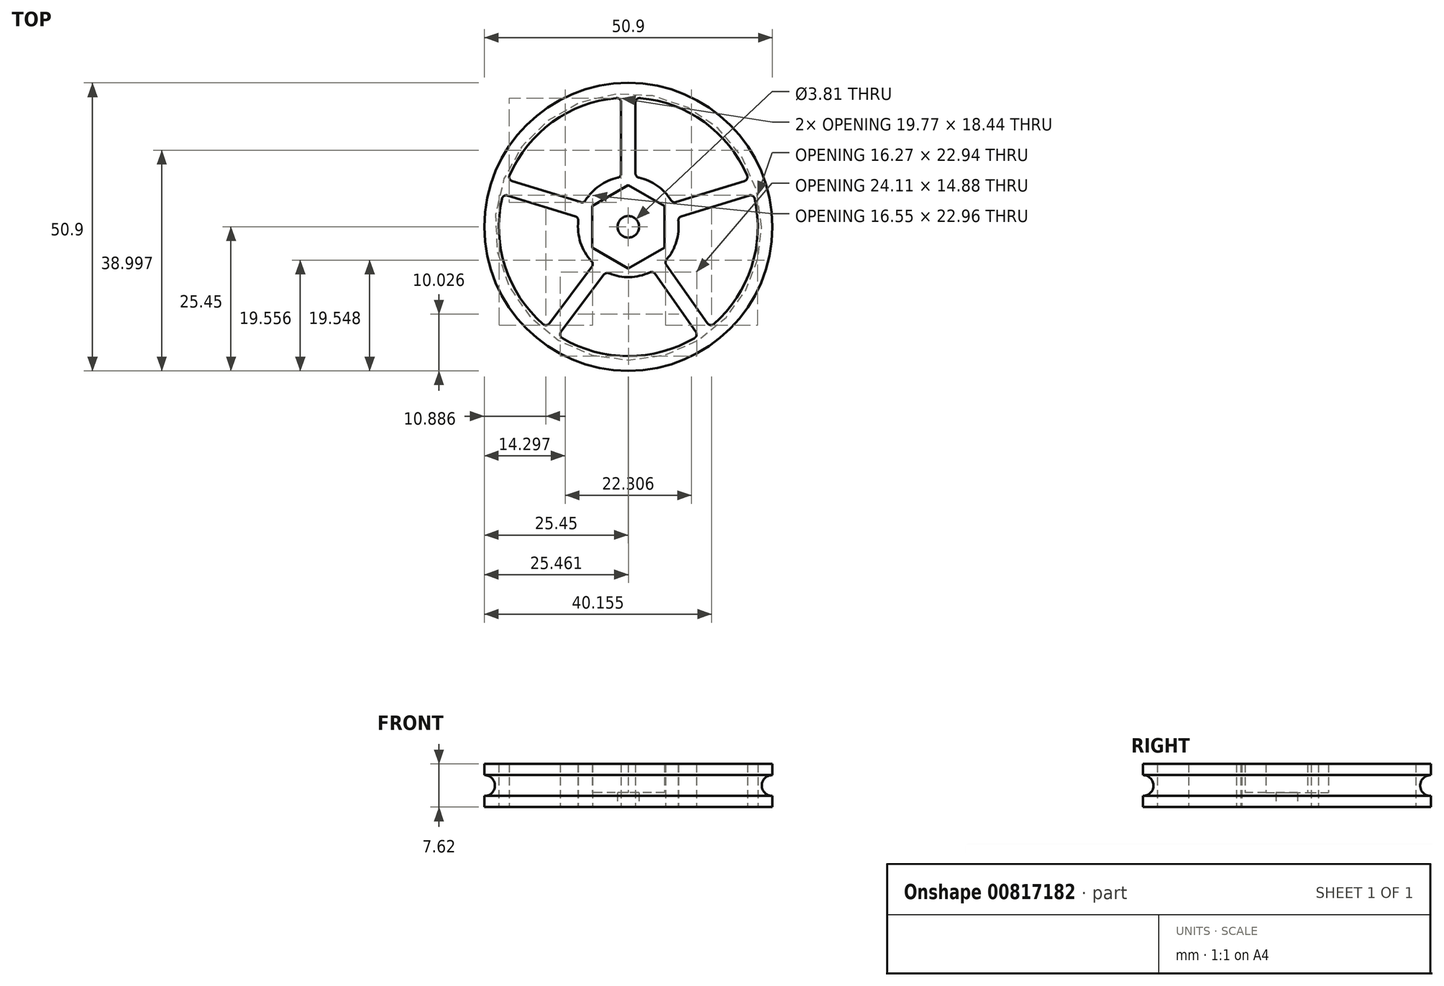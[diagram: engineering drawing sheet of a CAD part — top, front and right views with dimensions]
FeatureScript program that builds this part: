
annotation { "Feature Type Name" : "Feature", "Feature Type Description" : "" }
export const myFeature = defineFeature(function(context is Context, id is Id, definition is map)
    precondition{}
    {
        {
            var Q0;
            Q0=qCreatedBy(makeId("Top.planeOp"),FACE);
            var sketch = newSketch(context, id + "F0", { "sketchPlane" : qUnion([Q0])});
            skCircle(sketch, "E0", {"center": v(0, 0) * mm, "radius": 25.45 * mm});
            skArc(sketch, "E1", {"start": v(-22.32, 4.98) * mm, "mid": v(-21.74, -7.1) * mm, "end": v(-15.07, -17.2) * mm});
            skArc(sketch, "E2", {"start": v(-1.87, 8.7) * mm, "mid": v(-5.12, 7.27) * mm, "end": v(-7.56, 4.69) * mm});
            skArc(sketch, "E3.cCircle", {"start": v(-22.12, 5.78) * mm, "mid": v(-21.74, -7.1) * mm, "end": v(-14.45, -17.72) * mm, "construction": true});
            skLineSegment(sketch, "E4", {"start": v(1.27, 22.01) * mm, "end": v(1.27, 9.44) * mm});
            skLineSegment(sketch, "E5.MirrorCS", {"start": v(-1.27, 22.01) * mm, "end": v(-1.27, 9.44) * mm});
            skLineSegment(sketch, "E6", {"start": v(8.43, 4.36) * mm, "end": v(20.5, 8.08) * mm});
            skLineSegment(sketch, "E7", {"start": v(6.7, -6.72) * mm, "end": v(13.97, -17.04) * mm});
            skLineSegment(sketch, "E8", {"start": v(-4.32, -8.45) * mm, "end": v(-11.9, -18.55) * mm});
            skLineSegment(sketch, "E9", {"start": v(-8.43, 4.36) * mm, "end": v(-20.5, 8.08) * mm});
            skLineSegment(sketch, "E10.MirrorCS", {"start": v(9.36, 1.85) * mm, "end": v(21.35, 5.55) * mm});
            skLineSegment(sketch, "E11.MirrorCS", {"start": v(4.72, -8.3) * mm, "end": v(11.93, -18.56) * mm});
            skLineSegment(sketch, "E12.MirrorCS", {"start": v(-6.44, -7.05) * mm, "end": v(-13.96, -17.08) * mm});
            skLineSegment(sketch, "E13.MirrorCS", {"start": v(-9.36, 1.85) * mm, "end": v(-21.35, 5.55) * mm});
            skArc(sketch, "E14.trimOffspring", {"start": v(-1.27, 22.83) * mm, "mid": v(-13.41, 18.52) * mm, "end": v(-21.3, 8.32) * mm, "construction": true});
            skArc(sketch, "E15.trimOffspring", {"start": v(7.56, 4.69) * mm, "mid": v(5.12, 7.27) * mm, "end": v(1.87, 8.7) * mm});
            skArc(sketch, "E16.trimOffspring", {"start": v(21.3, 8.32) * mm, "mid": v(13.41, 18.52) * mm, "end": v(1.27, 22.83) * mm, "construction": true});
            skArc(sketch, "E17.trimOffspring", {"start": v(14.45, -17.72) * mm, "mid": v(21.74, -7.1) * mm, "end": v(22.12, 5.78) * mm, "construction": true});
            skArc(sketch, "E18.trimOffspring", {"start": v(6.75, -5.78) * mm, "mid": v(8.5, -2.6) * mm, "end": v(8.83, 1.04) * mm});
            skArc(sketch, "E19.trimOffspring", {"start": v(-3.41, -8.2) * mm, "mid": v(0.2, -8.89) * mm, "end": v(3.77, -8.05) * mm});
            skArc(sketch, "E20.trimOffspring", {"start": v(-12.4, -19.22) * mm, "mid": v(0, -22.87) * mm, "end": v(12.4, -19.22) * mm, "construction": true});
            skArc(sketch, "E21.trimOffspring", {"start": v(-8.83, 1.04) * mm, "mid": v(-8.45, -2.78) * mm, "end": v(-6.5, -6.07) * mm});
            skArc(sketch, "E22.trimOffspring", {"start": v(-11.67, -19.66) * mm, "mid": v(0.01, -22.87) * mm, "end": v(11.7, -19.65) * mm});
            skArc(sketch, "E23.trimOffspring", {"start": v(15.1, -17.18) * mm, "mid": v(21.74, -7.09) * mm, "end": v(22.32, 4.98) * mm});
            skArc(sketch, "E24.trimOffspring", {"start": v(20.97, 9.1) * mm, "mid": v(13.4, 18.52) * mm, "end": v(2.1, 22.77) * mm});
            skArc(sketch, "E25.trimOffspring", {"start": v(-2.1, 22.77) * mm, "mid": v(-13.4, 18.52) * mm, "end": v(-20.97, 9.1) * mm});
            skPoint(sketch, "E26.visualSharp", {"position": v(-1.27, 8.8) * mm});
            skArc(sketch, "E26.filletArc", {"start": v(-1.87, 8.7) * mm, "mid": v(-1.44, 8.96) * mm, "end": v(-1.27, 9.44) * mm});
            skPoint(sketch, "E27.visualSharp", {"position": v(1.27, 8.8) * mm});
            skArc(sketch, "E27.filletArc", {"start": v(1.27, 9.44) * mm, "mid": v(1.44, 8.96) * mm, "end": v(1.87, 8.7) * mm});
            skPoint(sketch, "E28.visualSharp", {"position": v(7.85, 4.18) * mm});
            skArc(sketch, "E28.filletArc", {"start": v(7.56, 4.69) * mm, "mid": v(7.94, 4.37) * mm, "end": v(8.43, 4.36) * mm});
            skPoint(sketch, "E29.visualSharp", {"position": v(8.73, 1.66) * mm});
            skArc(sketch, "E29.filletArc", {"start": v(9.36, 1.85) * mm, "mid": v(8.95, 1.54) * mm, "end": v(8.83, 1.04) * mm});
            skPoint(sketch, "E30.visualSharp", {"position": v(6.35, -6.22) * mm});
            skArc(sketch, "E30.filletArc", {"start": v(6.75, -5.78) * mm, "mid": v(6.57, -6.24) * mm, "end": v(6.7, -6.72) * mm});
            skPoint(sketch, "E31.visualSharp", {"position": v(4.34, -7.76) * mm});
            skArc(sketch, "E31.filletArc", {"start": v(4.72, -8.3) * mm, "mid": v(4.29, -8) * mm, "end": v(3.77, -8.05) * mm});
            skPoint(sketch, "E32.visualSharp", {"position": v(-3.95, -7.96) * mm});
            skArc(sketch, "E32.filletArc", {"start": v(-3.41, -8.2) * mm, "mid": v(-3.9, -8.18) * mm, "end": v(-4.32, -8.45) * mm});
            skPoint(sketch, "E33.visualSharp", {"position": v(-6.04, -6.52) * mm});
            skArc(sketch, "E33.filletArc", {"start": v(-6.44, -7.05) * mm, "mid": v(-6.29, -6.55) * mm, "end": v(-6.5, -6.07) * mm});
            skPoint(sketch, "E34.visualSharp", {"position": v(-8.73, 1.66) * mm});
            skArc(sketch, "E34.filletArc", {"start": v(-8.83, 1.04) * mm, "mid": v(-8.95, 1.54) * mm, "end": v(-9.36, 1.85) * mm});
            skPoint(sketch, "E35.visualSharp", {"position": v(-7.85, 4.18) * mm});
            skArc(sketch, "E35.filletArc", {"start": v(-8.43, 4.36) * mm, "mid": v(-7.94, 4.37) * mm, "end": v(-7.56, 4.69) * mm});
            skPoint(sketch, "E36.visualSharp", {"position": v(-1.27, 22.83) * mm});
            skArc(sketch, "E36.filletArc", {"start": v(-1.27, 22.01) * mm, "mid": v(-1.52, 22.57) * mm, "end": v(-2.1, 22.77) * mm});
            skPoint(sketch, "E37.visualSharp", {"position": v(1.27, 22.83) * mm});
            skArc(sketch, "E37.filletArc", {"start": v(2.1, 22.77) * mm, "mid": v(1.52, 22.57) * mm, "end": v(1.27, 22.01) * mm});
            skPoint(sketch, "E38.visualSharp", {"position": v(21.3, 8.32) * mm});
            skArc(sketch, "E38.filletArc", {"start": v(20.5, 8.08) * mm, "mid": v(20.97, 8.49) * mm, "end": v(20.97, 9.1) * mm});
            skPoint(sketch, "E39.visualSharp", {"position": v(22.12, 5.78) * mm});
            skArc(sketch, "E39.filletArc", {"start": v(22.32, 4.98) * mm, "mid": v(21.96, 5.48) * mm, "end": v(21.35, 5.55) * mm});
            skPoint(sketch, "E40.visualSharp", {"position": v(14.45, -17.72) * mm});
            skArc(sketch, "E40.filletArc", {"start": v(13.97, -17.04) * mm, "mid": v(14.5, -17.36) * mm, "end": v(15.1, -17.18) * mm});
            skPoint(sketch, "E41.visualSharp", {"position": v(12.4, -19.22) * mm});
            skArc(sketch, "E41.filletArc", {"start": v(11.7, -19.65) * mm, "mid": v(12.05, -19.15) * mm, "end": v(11.93, -18.56) * mm});
            skPoint(sketch, "E42.visualSharp", {"position": v(-12.4, -19.22) * mm});
            skArc(sketch, "E42.filletArc", {"start": v(-11.9, -18.55) * mm, "mid": v(-12.03, -19.16) * mm, "end": v(-11.67, -19.66) * mm});
            skPoint(sketch, "E43.visualSharp", {"position": v(-14.45, -17.72) * mm});
            skArc(sketch, "E43.filletArc", {"start": v(-15.07, -17.2) * mm, "mid": v(-14.5, -17.38) * mm, "end": v(-13.96, -17.08) * mm});
            skPoint(sketch, "E44.visualSharp", {"position": v(-22.12, 5.78) * mm});
            skArc(sketch, "E44.filletArc", {"start": v(-21.35, 5.55) * mm, "mid": v(-21.96, 5.48) * mm, "end": v(-22.32, 4.98) * mm});
            skPoint(sketch, "E45.visualSharp", {"position": v(-21.3, 8.32) * mm});
            skArc(sketch, "E45.filletArc", {"start": v(-20.97, 9.1) * mm, "mid": v(-20.97, 8.49) * mm, "end": v(-20.5, 8.08) * mm});
            skLineSegment(sketch, "E46.0", {"start": v(0, -7.37) * mm, "end": v(-6.38, -3.68) * mm});
            skLineSegment(sketch, "E46.1", {"start": v(-6.38, -3.68) * mm, "end": v(-6.38, 3.68) * mm});
            skLineSegment(sketch, "E46.2", {"start": v(-6.38, 3.68) * mm, "end": v(0, 7.37) * mm});
            skLineSegment(sketch, "E46.3", {"start": v(0, 7.37) * mm, "end": v(6.38, 3.68) * mm});
            skLineSegment(sketch, "E46.4", {"start": v(6.38, 3.68) * mm, "end": v(6.38, -3.68) * mm});
            skLineSegment(sketch, "E46.5", {"start": v(6.38, -3.68) * mm, "end": v(0, -7.37) * mm});
            skCircle(sketch, "E47", {"center": v(0, 0) * mm, "radius": 1.9 * mm});
            skSolve(sketch);
        }
        {
            var Q0;
            Q0=makeQuery(id+"F0.imprint","IMPRINT",FACE,{"disambiguationData":[TD([[makeQuery(id+"F0.imprint","IMPRINT",EDGE,{"derivedFrom":sQuery(id+"F0.wireOp",EDGE,"E0")}),1.0]])]});
            extrude(context, id + "F1", {"entities" : qUnion([Q0]), "depth" : 7.62 * mm, "offsetDistance" : 25.4 * mm});
        }
        {
            var Q0;
            Q0=makeQuery(id+"F0.imprint","IMPRINT",FACE,{"disambiguationData":[TD([[makeQuery(id+"F0.imprint","IMPRINT",EDGE,{"derivedFrom":sQuery(id+"F0.wireOp",EDGE,"E46.0")}),-1.0]])]});
            extrude(context, id + "F2", {"entities" : qUnion([Q0]), "operationType" : NewBodyOperationType.ADD, "depth" : 2.54 * mm, "offsetDistance" : 25.4 * mm});
        }
        {
            var Q0;
            Q0=qCreatedBy(makeId("Front.planeOp"),FACE);
            var sketch = newSketch(context, id + "F3", { "sketchPlane" : qUnion([Q0])});
            skLineSegment(sketch, "E48", {"start": v(0, 35.4) * mm, "end": v(0, -38.05) * mm});
            skSolve(sketch);
        }
        {
            var Q0;
            Q0=qCreatedBy(makeId("Front.planeOp"),FACE);
            var sketch = newSketch(context, id + "F4", { "sketchPlane" : qUnion([Q0])});
            skCircle(sketch, "E49", {"center": v(25.4, 3.81) * mm, "radius": 1.84 * mm});
            skSolve(sketch);
        }
        {
            var Q0;
            Q0=makeQuery(id+"F4.imprint","IMPRINT",FACE,{"disambiguationData":[TD([[makeQuery(id+"F4.imprint","IMPRINT",EDGE,{"derivedFrom":sQuery(id+"F4.wireOp",EDGE,"E49")}),1.0]])]});
            var Q1;
            Q1=sQuery(id+"F3.wireOp",EDGE,"E48");
            revolve(context, id + "F5", {"surfaceOperationType" : NewSurfaceOperationType.NEW, "entities" : qUnion([Q0]), "axis" : qUnion([Q1]), "revolveType" : RevolveType.FULL});
        }
        {
            var Q0;
            Q0=makeQuery(id+"F5.opRevolve","SWEPT_BODY",BODY,{"disambiguationData":[OSD([sQuery(id+"F4.wireOp",EDGE,"E49")])]});
            var Q1;
            Q1=makeQuery(id+"F1.opExtrude","SWEPT_BODY",BODY,{"disambiguationData":[OSD([sQuery(id+"F0.wireOp",EDGE,"E0"),sQuery(id+"F0.wireOp",EDGE,"E1"),sQuery(id+"F0.wireOp",EDGE,"E2"),sQuery(id+"F0.wireOp",EDGE,"E4"),sQuery(id+"F0.wireOp",EDGE,"E5.MirrorCS"),sQuery(id+"F0.wireOp",EDGE,"E6"),sQuery(id+"F0.wireOp",EDGE,"E7"),sQuery(id+"F0.wireOp",EDGE,"E8"),sQuery(id+"F0.wireOp",EDGE,"E9"),sQuery(id+"F0.wireOp",EDGE,"E10.MirrorCS"),sQuery(id+"F0.wireOp",EDGE,"E11.MirrorCS"),sQuery(id+"F0.wireOp",EDGE,"E12.MirrorCS"),sQuery(id+"F0.wireOp",EDGE,"E13.MirrorCS"),sQuery(id+"F0.wireOp",EDGE,"E15.trimOffspring"),sQuery(id+"F0.wireOp",EDGE,"E18.trimOffspring"),sQuery(id+"F0.wireOp",EDGE,"E19.trimOffspring"),sQuery(id+"F0.wireOp",EDGE,"E21.trimOffspring"),sQuery(id+"F0.wireOp",EDGE,"E22.trimOffspring"),sQuery(id+"F0.wireOp",EDGE,"E23.trimOffspring"),sQuery(id+"F0.wireOp",EDGE,"E24.trimOffspring"),sQuery(id+"F0.wireOp",EDGE,"E25.trimOffspring"),sQuery(id+"F0.wireOp",EDGE,"E26.filletArc"),sQuery(id+"F0.wireOp",EDGE,"E27.filletArc"),sQuery(id+"F0.wireOp",EDGE,"E28.filletArc"),sQuery(id+"F0.wireOp",EDGE,"E29.filletArc"),sQuery(id+"F0.wireOp",EDGE,"E30.filletArc"),sQuery(id+"F0.wireOp",EDGE,"E31.filletArc"),sQuery(id+"F0.wireOp",EDGE,"E32.filletArc"),sQuery(id+"F0.wireOp",EDGE,"E33.filletArc"),sQuery(id+"F0.wireOp",EDGE,"E34.filletArc"),sQuery(id+"F0.wireOp",EDGE,"E35.filletArc"),sQuery(id+"F0.wireOp",EDGE,"E36.filletArc"),sQuery(id+"F0.wireOp",EDGE,"E37.filletArc"),sQuery(id+"F0.wireOp",EDGE,"E38.filletArc"),sQuery(id+"F0.wireOp",EDGE,"E39.filletArc"),sQuery(id+"F0.wireOp",EDGE,"E40.filletArc"),sQuery(id+"F0.wireOp",EDGE,"E41.filletArc"),sQuery(id+"F0.wireOp",EDGE,"E42.filletArc"),sQuery(id+"F0.wireOp",EDGE,"E43.filletArc"),sQuery(id+"F0.wireOp",EDGE,"E44.filletArc"),sQuery(id+"F0.wireOp",EDGE,"E45.filletArc"),sQuery(id+"F0.wireOp",EDGE,"E46.0"),sQuery(id+"F0.wireOp",EDGE,"E46.1"),sQuery(id+"F0.wireOp",EDGE,"E46.2"),sQuery(id+"F0.wireOp",EDGE,"E46.3"),sQuery(id+"F0.wireOp",EDGE,"E46.4"),sQuery(id+"F0.wireOp",EDGE,"E46.5")])]});
            booleanBodies(context, id + "F6", {"operationType" : BooleanOperationType.SUBTRACTION, "tools" : qUnion([Q0]), "targets" : qUnion([Q1])});
        }
    });
